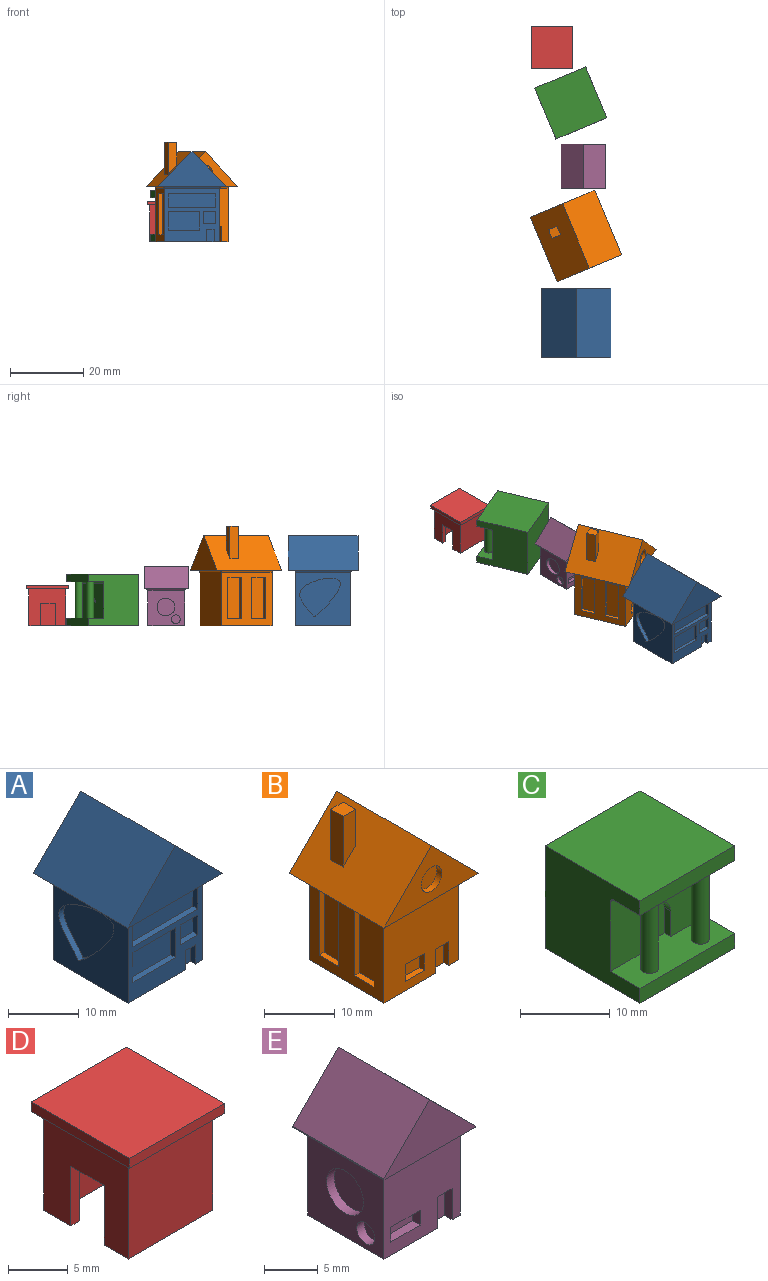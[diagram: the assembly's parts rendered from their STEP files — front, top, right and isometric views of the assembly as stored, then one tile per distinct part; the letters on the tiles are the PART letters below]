
ASSEMBLY  parts=5 mates=4
PART A: 42 faces, bbox 19x19x24.5 mm
  f0: plane 15x14.5mm, normal (1,0,0), area 123.9mm2, adj f2,f3,f4,f13,f35,f36,f37,f38
  f1: plane 15x14.5mm, normal (-1,0,0), area 145.3mm2, adj f2,f3,f4,f10,f33
  f2: plane 15x14.5mm, normal (0,-1,0), area 106.4mm2, adj f0,f1,f4,f12,f14,f15,f16,f18
  f3: plane 15x14.5mm, normal (0,1,0), area 217.5mm2, adj f0,f1,f4,f11
  f4: plane 15x15mm, normal (0,0,-1), area 223mm2, adj f0,f1,f2,f3,f14,f15,f17
  f5: plane 19x19mm, normal (0,0,-1), area 105mm2, adj f6,f7,f8,f9,f10,f11,f12,f13
  f6: plane 19x9.5mm, normal (0,-1,0), area 90.3mm2, adj f5,f8,f9
  f7: plane 19x9.5mm, normal (0,1,0), area 90.3mm2, adj f5,f8,f9
  f8: plane 19x9.5mm, normal (0.71,0,0.71), area 255.3mm2, adj f5,f6,f7,f9
  f9: plane 19x9.5mm, normal (-0.71,0,0.71), area 255.3mm2, adj f5,f6,f7,f8
  f10: cylinder r=0.5mm len=16mm, axis (0,1,0), area 12.1mm2, adj f1,f5,f11,f12
  f11: cylinder r=0.5mm len=16mm, axis (1,0,0), area 12.1mm2, adj f3,f5,f10,f13
  f12: cylinder r=0.5mm len=16mm, axis (-1,0,0), area 12.1mm2, adj f2,f5,f10,f13
  f13: cylinder r=0.5mm len=16mm, axis (0,-1,0), area 12.1mm2, adj f0,f5,f11,f12
  f14: plane 3.33x1mm, normal (1,0,0), area 3.3mm2, adj f2,f4,f16,f17
  f15: plane 3.33x1mm, normal (-1,0,0), area 3.3mm2, adj f2,f4,f16,f17
  f16: plane 2x1mm, normal (0,0,-1), area 2mm2, adj f2,f14,f15,f17
  f17: plane 3.33x2mm, normal (0,-1,0), area 6.7mm2, adj f4,f14,f15,f16
  f18: plane 5.15x1mm, normal (-1,0,0), area 5.2mm2, adj f2,f19,f21,f22
  f19: plane 8.5x1mm, normal (0,0,-1), area 8.5mm2, adj f2,f18,f20,f22
  f20: plane 5.15x1mm, normal (1,0,0), area 5.2mm2, adj f2,f19,f21,f22
  f21: plane 8.5x1mm, normal (0,0,1), area 8.5mm2, adj f2,f18,f20,f22
  f22: plane 8.5x5.15mm, normal (0,-1,0), area 43.8mm2, adj f18,f19,f20,f21
  f23: plane 3.74x1mm, normal (1,0,0), area 3.7mm2, adj f2,f24,f26,f27
  f24: plane 13x1mm, normal (0,0,1), area 13mm2, adj f2,f23,f25,f27
  f25: plane 3.74x1mm, normal (-1,0,0), area 3.7mm2, adj f2,f24,f26,f27
  f26: plane 13x1mm, normal (0,0,-1), area 13mm2, adj f2,f23,f25,f27
  f27: plane 13x3.74mm, normal (0,-1,0), area 48.6mm2, adj f23,f24,f25,f26
  f28: plane 3.45x1mm, normal (1,0,0), area 3.5mm2, adj f2,f29,f31,f32
  f29: plane 3.5x1mm, normal (0,0,1), area 3.5mm2, adj f2,f28,f30,f32
  f30: plane 3.45x1mm, normal (-1,0,0), area 3.4mm2, adj f2,f29,f31,f32,f39,f40
  f31: plane 3.5x1mm, normal (0,0,-1), area 3.5mm2, adj f2,f28,f30,f32,f41
  f32: plane 3.5x3.45mm, normal (0,-1,0), area 12.1mm2, adj f28,f29,f30,f31,f41
  f33: extruded ~11.06x10.43mm, area 32.7mm2, adj f1,f34
  f34: plane 12.46x11.98mm, normal (-1,0,0), area 72.2mm2, adj f33
  f35: plane 5.81x1.52mm, normal (0,0.25,0.97), area 6mm2, adj f0,f36,f40,f41
  f36: plane 4.27x4.22mm, normal (0,-0.71,0.7), area 6mm2, adj f0,f35,f37,f41
  f37: plane 5.79x1.59mm, normal (0,-0.96,-0.26), area 6mm2, adj f0,f36,f38,f41
  f38: plane 5.81x1.52mm, normal (0,-0.25,-0.97), area 6mm2, adj f0,f37,f39,f41
  f39: plane 4.27x4.22mm, normal (0,0.71,-0.7), area 6mm2, adj f0,f30,f38,f40,f41
  f40: plane 5.79x1.59mm, normal (0,0.96,0.26), area 6mm2, adj f0,f30,f35,f39,f41
  f41: plane 11.58x11.55mm, normal (1,0,0), area 93.6mm2, adj f31,f32,f35,f36,f37,f38,f39,f40
PART B: 49 faces, bbox 19x19x27 mm
  f0: plane 15x14.5mm, normal (1,0,0), area 160.4mm2, adj f9,f10,f11,f18,f19,f20
  f1: plane 2.5x2.5mm, normal (0,0,1), area 6.2mm2, adj f2,f3,f4,f5
  f2: plane 8.75x2.5mm, normal (0,1,0), area 18.8mm2, adj f1,f3,f5,f14
  f3: plane 6.25x2.5mm, normal (1,0,0), area 15.6mm2, adj f1,f2,f4,f14
  f4: plane 8.75x2.5mm, normal (0,-1,0), area 18.8mm2, adj f1,f3,f5,f14
  f5: plane 8.75x2.5mm, normal (-1,0,0), area 21.9mm2, adj f1,f2,f4,f14
  f6: plane 19x19mm, normal (0,0,-1), area 105mm2, adj f7,f8,f13,f14,f15,f16,f17,f18
  f7: plane 19x9.5mm, normal (0,-1,0), area 76.8mm2, adj f6,f13,f14,f31
  f8: plane 19x9.5mm, normal (0,1,0), area 90.2mm2, adj f6,f13,f14
  f9: plane 15x15mm, normal (0,0,-1), area 222.4mm2, adj f0,f10,f11,f12,f27,f28,f30
  f10: plane 15x14.5mm, normal (0,1,0), area 217.5mm2, adj f0,f9,f12,f16
  f11: plane 15x14.5mm, normal (0,-1,0), area 195.4mm2, adj f0,f9,f12,f17,f22,f23,f24,f25
  f12: plane 15x14.5mm, normal (-1,0,0), area 128.5mm2, adj f9,f10,f11,f15,f33,f34,f35,f36
  f13: plane 19x9.5mm, normal (0.71,0,0.71), area 255.3mm2, adj f6,f7,f8,f14
  f14: plane 19x9.5mm, normal (-0.71,0,0.71), area 246.4mm2, adj f2,f3,f4,f5,f6,f7,f8,f13
  f15: cylinder r=0.5mm len=16mm, axis (0,1,0), area 12.1mm2, adj f6,f12,f16,f17
  f16: cylinder r=0.5mm len=16mm, axis (1,0,0), area 12.1mm2, adj f6,f10,f15,f18
  f17: cylinder r=0.5mm len=16mm, axis (-1,0,0), area 12.1mm2, adj f6,f11,f15,f18
  f18: cylinder r=0.5mm len=16mm, axis (0,-1,0), area 12.1mm2, adj f0,f6,f16,f17
  f19: cylinder r=2.79mm len=2.85mm, axis (1,0,0), area 4.2mm2, adj f0,f20,f21
  f20: cylinder r=4.38mm len=8.76mm, axis (1,0,0), area 23.6mm2, adj f0,f19,f21
  f21: plane 8.76x8.76mm, normal (1,0,0), area 57.1mm2, adj f19,f20
  f22: plane 2.93x1mm, normal (1,0,0), area 2.9mm2, adj f11,f23,f25,f26
  f23: plane 3.81x1mm, normal (0,0,1), area 3.8mm2, adj f11,f22,f24,f26
  f24: plane 2.93x1mm, normal (-1,0,0), area 2.9mm2, adj f11,f23,f25,f26
  f25: plane 3.81x1mm, normal (0,0,-1), area 3.8mm2, adj f11,f22,f24,f26
  f26: plane 3.81x2.93mm, normal (0,-1,0), area 11.2mm2, adj f22,f23,f24,f25
  f27: plane 4.15x1mm, normal (1,0,0), area 4.2mm2, adj f9,f11,f29,f30
  f28: plane 4.15x1mm, normal (-1,0,0), area 4.2mm2, adj f9,f11,f29,f30
  f29: plane 2.65x1mm, normal (0,0,-1), area 2.6mm2, adj f11,f27,f28,f30
  f30: plane 4.15x2.65mm, normal (0,-1,0), area 11mm2, adj f9,f27,f28,f29
  f31: cylinder r=2.07mm len=4.14mm, axis (0,-1,0), area 13mm2, adj f7,f32
  f32: plane 4.14x4.14mm, normal (0,-1,0), area 13.4mm2, adj f31
  f33: plane 11.28x1mm, normal (0,-1,0), area 11.3mm2, adj f12,f34,f36,f37
  f34: plane 3.95x1mm, normal (0,0,1), area 3.9mm2, adj f12,f33,f35,f37
  f35: plane 11.28x1mm, normal (0,1,0), area 11.3mm2, adj f12,f34,f36,f37
  f36: plane 3.95x1mm, normal (0,0,-1), area 3.9mm2, adj f12,f33,f35,f37
  f37: plane 11.28x3.95mm, normal (-1,0,0), area 44.5mm2, adj f33,f34,f35,f36
  f38: plane 11.28x1mm, normal (0,-1,0), area 11.3mm2, adj f12,f39,f41,f42
  f39: plane 3.95x1mm, normal (0,0,1), area 3.9mm2, adj f12,f38,f40,f42
  f40: plane 11.28x1mm, normal (0,1,0), area 11.3mm2, adj f12,f39,f41,f42
  f41: plane 3.95x1mm, normal (0,0,-1), area 3.9mm2, adj f12,f38,f40,f42
  f42: plane 11.28x3.95mm, normal (-1,0,0), area 44.5mm2, adj f38,f39,f40,f41
  f43: plane 1.5x1.5mm, normal (0,0,1), area 2.2mm2, adj f44,f45,f46,f47
  f44: plane 5x1.5mm, normal (0,1,0), area 7.5mm2, adj f43,f45,f47,f48
  f45: plane 5x1.5mm, normal (-1,0,0), area 7.5mm2, adj f43,f44,f46,f48
  f46: plane 5x1.5mm, normal (0,-1,0), area 7.5mm2, adj f43,f45,f47,f48
  f47: plane 5x1.5mm, normal (1,0,0), area 7.5mm2, adj f43,f44,f46,f48
  f48: plane 1.5x1.5mm, normal (0,0,-1), area 2.2mm2, adj f44,f45,f46,f47
PART C: 17 faces, bbox 15x15x14 mm
  f0: plane 15x14mm, normal (-1,0,0), area 163.4mm2, adj f1,f3,f4,f5,f6,f9,f10,f11
  f1: plane 15x2mm, normal (0,-1,0), area 30mm2, adj f0,f2,f4,f5
  f2: plane 15x14mm, normal (1,0,0), area 163.4mm2, adj f1,f3,f4,f5,f6,f9,f10,f11
  f3: plane 15x14mm, normal (0,1,0), area 210mm2, adj f0,f2,f5,f10
  f4: plane 15x5.66mm, normal (0,0,1), area 67.7mm2, adj f0,f1,f2,f6,f7,f8,f13,f15
  f5: plane 15x15mm, normal (0,0,-1), area 225mm2, adj f0,f1,f2,f3
  f6: plane 15x9.5mm, normal (0,-1,0), area 122.2mm2, adj f0,f2,f4,f12,f13,f14,f15
  f7: cylinder r=1mm len=10mm, axis (0,0,-1), area 62.8mm2, adj f4,f11
  f8: cylinder r=1mm len=10mm, axis (0,0,-1), area 62.8mm2, adj f4,f11
  f9: plane 15x2mm, normal (0,-1,0), area 30mm2, adj f0,f2,f10,f11
  f10: plane 15x15mm, normal (0,0,1), area 225mm2, adj f0,f2,f3,f9
  f11: plane 15x4.16mm, normal (0,0,-1), area 56.2mm2, adj f0,f2,f7,f8,f9,f12
  f12: cylinder r=0.5mm len=15mm, axis (-1,0,0), area 11.8mm2, adj f0,f2,f6,f11
  f13: plane 3.5x1mm, normal (-1,0,0), area 3.5mm2, adj f4,f6,f14,f16
  f14: cylinder r=2mm len=4mm, axis (0,-1,0), area 6.3mm2, adj f6,f13,f15,f16
  f15: plane 3.5x1mm, normal (1,0,0), area 3.5mm2, adj f4,f6,f14,f16
  f16: plane 5.5x4mm, normal (0,-1,0), area 20.3mm2, adj f4,f13,f14,f15
PART D: 19 faces, bbox 11.2x11.6x11 mm
  f0: plane 10x10mm, normal (-1,0,0), area 76mm2, adj f1,f3,f4,f10,f11,f12,f13
  f1: plane 10x10mm, normal (0,-1,0), area 100mm2, adj f0,f2,f4,f13
  f2: plane 10x10mm, normal (1,0,0), area 100mm2, adj f1,f3,f4,f13
  f3: plane 10x10mm, normal (0,1,0), area 100mm2, adj f0,f2,f4,f13
  f4: plane 10x10mm, normal (0,0,-1), area 32.1mm2, adj f0,f1,f2,f3,f5,f6,f7,f8
  f5: plane 9x8mm, normal (1,0,0), area 48mm2, adj f4,f6,f8,f9,f10,f11,f12
  f6: plane 9x8mm, normal (0,1,0), area 72mm2, adj f4,f5,f7,f9
  f7: plane 9x8mm, normal (-1,0,0), area 72mm2, adj f4,f6,f8,f9
  f8: plane 9x8mm, normal (0,-1,0), area 72mm2, adj f4,f5,f7,f9
  f9: plane 8x8mm, normal (0,0,-1), area 64mm2, adj f5,f6,f7,f8
  f10: plane 6.1x1mm, normal (0,1,0), area 6.1mm2, adj f0,f4,f5,f11
  f11: plane 3.93x1mm, normal (0,0,-1), area 3.9mm2, adj f0,f5,f10,f12
  f12: plane 6.1x1mm, normal (0,-1,0), area 6.1mm2, adj f0,f4,f5,f11
  f13: plane 11.58x11.24mm, normal (0,0,-1), area 30.1mm2, adj f0,f1,f2,f3,f14,f15,f16,f17
  f14: plane 11.58x1mm, normal (1,0,0), area 11.6mm2, adj f13,f15,f17,f18
  f15: plane 11.24x1mm, normal (0,1,0), area 11.2mm2, adj f13,f14,f16,f18
  f16: plane 11.58x1mm, normal (-1,0,0), area 11.6mm2, adj f13,f15,f17,f18
  f17: plane 11.24x1mm, normal (0,-1,0), area 11.2mm2, adj f13,f14,f16,f18
  f18: plane 11.58x11.24mm, normal (0,0,1), area 130.1mm2, adj f14,f15,f16,f17
PART E: 39 faces, bbox 12x12x16.1 mm
  f0: plane 10x9.5mm, normal (0,-1,0), area 81.5mm2, adj f1,f2,f4,f14,f16,f17,f18,f20
  f1: plane 10x9.5mm, normal (-1,0,0), area 72.2mm2, adj f0,f3,f4,f12,f35,f37
  f2: plane 10x9.5mm, normal (1,0,0), area 82.9mm2, adj f0,f3,f4,f15,f25,f26,f27,f28
  f3: plane 10x9.5mm, normal (0,1,0), area 95mm2, adj f1,f2,f4,f13
  f4: plane 10x10mm, normal (0,0,-1), area 98.1mm2, adj f0,f1,f2,f3,f16,f18,f19
  f5: plane 12x12mm, normal (0,0,-1), area 23mm2, adj f6,f7,f8,f9,f12,f13,f14,f15
  f6: plane 12x0.1mm, normal (-1,0,0), area 1.2mm2, adj f5,f7,f9,f11
  f7: plane 12x6.1mm, normal (0,-1,0), area 37.2mm2, adj f5,f6,f8,f10,f11
  f8: plane 12x0.1mm, normal (1,0,0), area 1.2mm2, adj f5,f7,f9,f10
  f9: plane 12x6.1mm, normal (0,1,0), area 37.2mm2, adj f5,f6,f8,f10,f11
  f10: plane 12x6mm, normal (0.71,0,0.71), area 101.8mm2, adj f7,f8,f9,f11
  f11: plane 12x6mm, normal (-0.71,0,0.71), area 101.8mm2, adj f6,f7,f9,f10
  f12: cylinder r=0.5mm len=11mm, axis (0,1,0), area 8.1mm2, adj f1,f5,f13,f14
  f13: cylinder r=0.5mm len=11mm, axis (1,0,0), area 8.1mm2, adj f3,f5,f12,f15
  f14: cylinder r=0.5mm len=11mm, axis (-1,0,0), area 8.1mm2, adj f0,f5,f12,f15
  f15: cylinder r=0.5mm len=11mm, axis (0,-1,0), area 8.1mm2, adj f2,f5,f13,f14
  f16: plane 3.54x1mm, normal (-1,0,0), area 3.5mm2, adj f0,f4,f17,f19
  f17: plane 1.93x1mm, normal (0,0,-1), area 1.9mm2, adj f0,f16,f18,f19
  f18: plane 3.54x1mm, normal (1,0,0), area 3.5mm2, adj f0,f4,f17,f19
  f19: plane 3.54x1.93mm, normal (0,-1,0), area 6.8mm2, adj f4,f16,f17,f18
  f20: plane 1.69x1mm, normal (1,0,0), area 1.7mm2, adj f0,f21,f23,f24
  f21: plane 3.91x1mm, normal (0,0,1), area 3.9mm2, adj f0,f20,f22,f24
  f22: plane 1.69x1mm, normal (-1,0,0), area 1.7mm2, adj f0,f21,f23,f24
  f23: plane 3.91x1mm, normal (0,0,-1), area 3.9mm2, adj f0,f20,f22,f24
  f24: plane 3.91x1.69mm, normal (0,-1,0), area 6.6mm2, adj f20,f21,f22,f23
  f25: plane 2.8x1mm, normal (0,1,0), area 2.8mm2, adj f2,f26,f28,f29
  f26: plane 2.1x1mm, normal (0,0,1), area 2.1mm2, adj f2,f25,f27,f29
  f27: plane 2.8x1mm, normal (0,-1,0), area 2.8mm2, adj f2,f26,f28,f29
  f28: plane 2.1x1mm, normal (0,0,-1), area 2.1mm2, adj f2,f25,f27,f29
  f29: plane 2.8x2.1mm, normal (1,0,0), area 5.9mm2, adj f25,f26,f27,f28
  f30: plane 2.8x1mm, normal (0,1,0), area 2.8mm2, adj f2,f31,f33,f34
  f31: plane 2.2x1mm, normal (0,0,1), area 2.2mm2, adj f2,f30,f32,f34
  f32: plane 2.8x1mm, normal (0,-1,0), area 2.8mm2, adj f2,f31,f33,f34
  f33: plane 2.2x1mm, normal (0,0,-1), area 2.2mm2, adj f2,f30,f32,f34
  f34: plane 2.8x2.2mm, normal (1,0,0), area 6.2mm2, adj f30,f31,f32,f33
  f35: cylinder r=2.41mm len=4.82mm, axis (-1,0,0), area 15.1mm2, adj f1,f36
  f36: plane 4.82x4.82mm, normal (-1,0,0), area 18.2mm2, adj f35
  f37: cylinder r=1.2mm len=2.4mm, axis (-1,0,0), area 7.5mm2, adj f1,f38
  f38: plane 2.4x2.4mm, normal (-1,0,0), area 4.5mm2, adj f37
PLACE A rot(axis=(0.55,0.74,-0.39),0deg) t=(12.19,3.18,-5.27)mm
PLACE B rot(axis=(0,0,1),22.5deg) t=(-67.27,16.82,-5.27)mm
PLACE C rot(axis=(0,0,-1),157.5deg) t=(-26.47,42.51,-5.27)mm
PLACE D t=(5.58,17.3,-5.27)mm
PLACE E rot(axis=(0.55,0.74,-0.39),0deg) t=(-64.48,-18.34,-5.27)mm
MATE planar B.f9 <-> E.f4  axis (0,0,-1) through (-25.38,6.66,-5.27)mm
MATE planar B.f9 <-> C.f5  axis (0,0,-1) through (-25.38,6.66,-5.27)mm
MATE planar A.f4 <-> B.f9  axis (0,0,-1) through (-25.34,-17.04,-5.27)mm
MATE planar E.f4 <-> D.f4  axis (0,0,-1) through (-23.43,25.68,-5.27)mm
